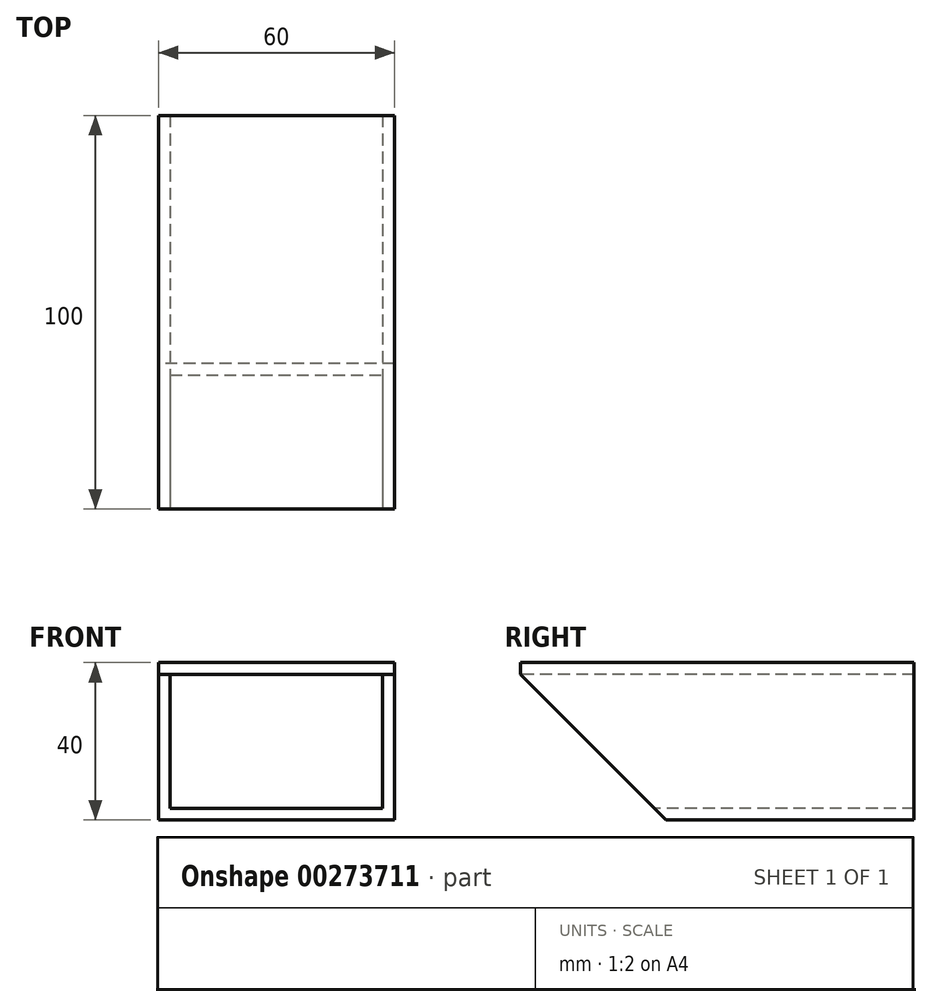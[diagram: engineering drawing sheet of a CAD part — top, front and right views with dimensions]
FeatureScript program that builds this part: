
annotation { "Feature Type Name" : "Feature", "Feature Type Description" : "" }
export const myFeature = defineFeature(function(context is Context, id is Id, definition is map)
    precondition{}
    {
        {
            var Q0;
            Q0=qCreatedBy(makeId("Top.planeOp"),FACE);
            var sketch = newSketch(context, id + "F0", { "sketchPlane" : qUnion([Q0])});
            skLineSegment(sketch, "E0.bottom", {"start": v(30, 50) * mm, "end": v(-30, 50) * mm});
            skLineSegment(sketch, "E0.top", {"start": v(30, -50) * mm, "end": v(-30, -50) * mm});
            skLineSegment(sketch, "E0.left", {"start": v(30, 50) * mm, "end": v(30, -50) * mm});
            skLineSegment(sketch, "E0.right", {"start": v(-30, 50) * mm, "end": v(-30, -50) * mm});
            skPoint(sketch, "E0.middle", {"position": v(0, 0) * mm});
            skSolve(sketch);
        }
        {
            var Q0;
            Q0 = qSketchRegion(id + "F0", true);
            var Q1;
            Q1=makeQuery(id+"F0.imprint","IMPRINT",FACE,{"disambiguationData":[TD([[makeQuery(id+"F0.imprint","IMPRINT",EDGE,{"derivedFrom":sQuery(id+"F0.wireOp",EDGE,"E0.bottom")}),1.0]])]});
            extrude(context, id + "F1", {"entities" : qUnion([Q0, Q1]), "depth" : 40 * mm});
        }
        {
            var Q0;
            Q0=makeQuery(id+"F1.opExtrude","SWEPT_FACE",FACE,{"disambiguationData":[OSD([sQuery(id+"F0.wireOp",EDGE,"E0.top")])]});
            var sketch = newSketch(context, id + "F2", { "sketchPlane" : qUnion([Q0])});
            skLineSegment(sketch, "E1.bottom", {"start": v(27, 37) * mm, "end": v(-27, 37) * mm});
            skLineSegment(sketch, "E1.top", {"start": v(27, 3) * mm, "end": v(-27, 3) * mm});
            skLineSegment(sketch, "E1.left", {"start": v(27, 37) * mm, "end": v(27, 3) * mm});
            skLineSegment(sketch, "E1.right", {"start": v(-27, 37) * mm, "end": v(-27, 3) * mm});
            skPoint(sketch, "E1.middle", {"position": v(0, 20) * mm});
            skPoint(sketch, "E1.middle.positionSnap0", {"position": v(30, 20) * mm});
            skPoint(sketch, "E1.centerSnap0", {"position": v(30, 20) * mm});
            skSolve(sketch);
        }
        {
            var Q0;
            Q0=makeQuery(id+"F2.imprint","IMPRINT",FACE,{"disambiguationData":[TD([[makeQuery(id+"F2.imprint","IMPRINT",EDGE,{"derivedFrom":sQuery(id+"F2.wireOp",EDGE,"E1.bottom")}),1.0]])]});
            extrude(context, id + "F3", {"entities" : qUnion([Q0]), "operationType" : NewBodyOperationType.REMOVE, "oppositeDirection" : true, "depth" : 141 * mm});
        }
        {
            var Q0;
            Q0=makeQuery(id+"F1.opExtrude","SWEPT_FACE",FACE,{"disambiguationData":[OSD([sQuery(id+"F0.wireOp",EDGE,"E0.right")])]});
            var sketch = newSketch(context, id + "F4", { "sketchPlane" : qUnion([Q0])});
            skPoint(sketch, "E2", {"position": v(13, 0) * mm});
            skPoint(sketch, "E3", {"position": v(50, 37) * mm});
            skLineSegment(sketch, "E4", {"start": v(13, 0) * mm, "end": v(50, 37) * mm});
            skLineSegment(sketch, "E5", {"start": v(50, 0) * mm, "end": v(13, 0) * mm});
            skLineSegment(sketch, "E6", {"start": v(50, 0) * mm, "end": v(50, 37) * mm});
            skSolve(sketch);
        }
        {
            var Q0;
            Q0=makeQuery(id+"F4.imprint","IMPRINT",FACE,{"disambiguationData":[TD([[makeQuery(id+"F4.imprint","IMPRINT",EDGE,{"derivedFrom":sQuery(id+"F4.wireOp",EDGE,"E4")}),-1.0]])]});
            extrude(context, id + "F5", {"entities" : qUnion([Q0]), "operationType" : NewBodyOperationType.REMOVE, "oppositeDirection" : true, "depth" : 60 * mm});
        }
    });
